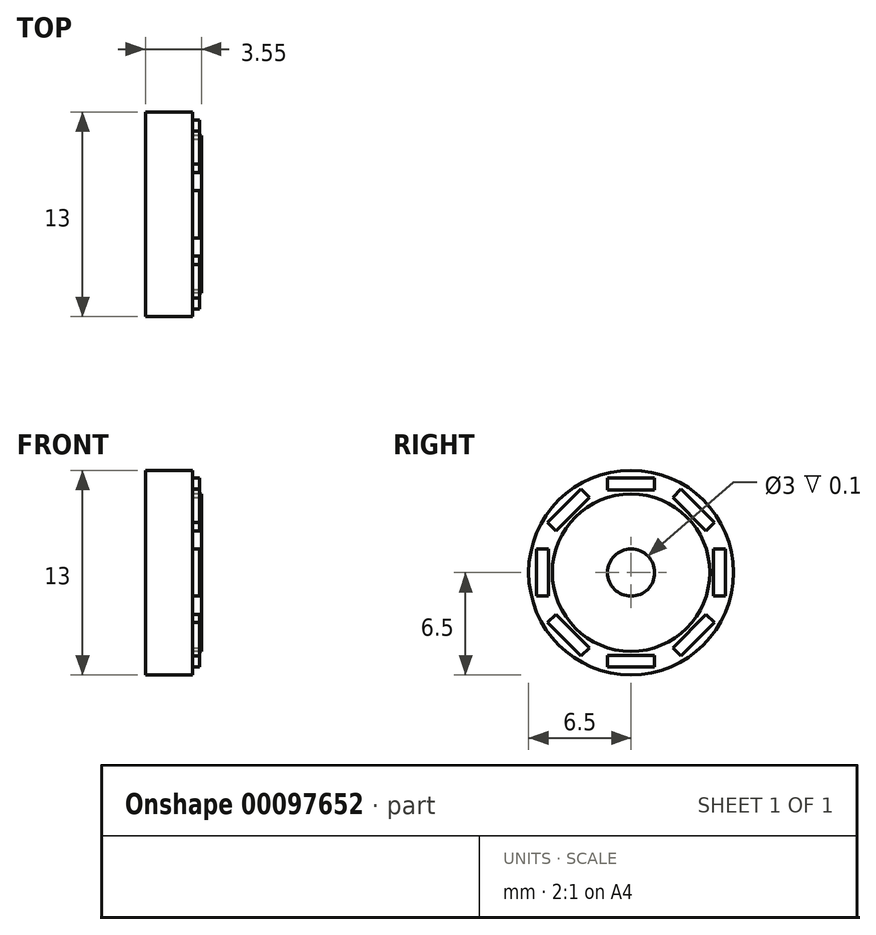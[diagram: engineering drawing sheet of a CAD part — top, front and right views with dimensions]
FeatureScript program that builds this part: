
annotation { "Feature Type Name" : "Feature", "Feature Type Description" : "" }
export const myFeature = defineFeature(function(context is Context, id is Id, definition is map)
    precondition{}
    {
        {
            var Q0;
            Q0=qCreatedBy(makeId("Right.planeOp"),FACE);
            var sketch = newSketch(context, id + "F0", { "sketchPlane" : qUnion([Q0])});
            skCircle(sketch, "E0", {"center": v(0, 0) * mm, "radius": 6.5 * mm});
            skCircle(sketch, "E1", {"center": v(0, 0) * mm, "radius": 5 * mm});
            skCircle(sketch, "E2", {"center": v(0, 0) * mm, "radius": 1.5 * mm});
            skSolve(sketch);
        }
        {
            var Q0;
            Q0=makeQuery(id+"F0.imprint","IMPRINT",FACE,{"disambiguationData":[TD([[makeQuery(id+"F0.imprint","IMPRINT",EDGE,{"derivedFrom":sQuery(id+"F0.wireOp",EDGE,"E0")}),1.0]])]});
            var Q1;
            Q1=makeQuery(id+"F0.imprint","IMPRINT",FACE,{"disambiguationData":[TD([[makeQuery(id+"F0.imprint","IMPRINT",EDGE,{"derivedFrom":sQuery(id+"F0.wireOp",EDGE,"E1")}),1.0]])]});
            var Q2;
            Q2=makeQuery(id+"F0.imprint","IMPRINT",FACE,{"disambiguationData":[TD([[makeQuery(id+"F0.imprint","IMPRINT",EDGE,{"derivedFrom":sQuery(id+"F0.wireOp",EDGE,"E2")}),1.0]])]});
            extrude(context, id + "F1", {"entities" : qUnion([Q0, Q1, Q2]), "depth" : 3 * mm});
        }
        {
            var Q0;
            Q0=makeQuery(id+"F0.imprint","IMPRINT",FACE,{"disambiguationData":[TD([[makeQuery(id+"F0.imprint","IMPRINT",EDGE,{"derivedFrom":sQuery(id+"F0.wireOp",EDGE,"E1")}),1.0]])]});
            extrude(context, id + "F2", {"entities" : qUnion([Q0]), "operationType" : NewBodyOperationType.ADD, "depth" : 3.55 * mm});
        }
        {
            var Q0;
            Q0=makeQuery(id+"F0.imprint","IMPRINT",FACE,{"disambiguationData":[TD([[makeQuery(id+"F0.imprint","IMPRINT",EDGE,{"derivedFrom":sQuery(id+"F0.wireOp",EDGE,"E2")}),1.0]])]});
            extrude(context, id + "F3", {"entities" : qUnion([Q0]), "operationType" : NewBodyOperationType.ADD, "depth" : 3.45 * mm});
        }
        {
            var Q0;
            Q0=makeQuery(id+"F3.opExtrude","CAP_FACE",FACE,{"disambiguationData":[OSD([sQuery(id+"F0.wireOp",EDGE,"E2")])],"isStart":false});
            var sketch = newSketch(context, id + "F4", { "sketchPlane" : qUnion([Q0])});
            skLineSegment(sketch, "E3.bottom", {"start": v(-1.5, 6) * mm, "end": v(1.5, 6) * mm});
            skLineSegment(sketch, "E3.top", {"start": v(-1.5, 5.25) * mm, "end": v(1.5, 5.25) * mm});
            skLineSegment(sketch, "E3.left", {"start": v(-1.5, 6) * mm, "end": v(-1.5, 5.25) * mm});
            skLineSegment(sketch, "E3.right", {"start": v(1.5, 6) * mm, "end": v(1.5, 5.25) * mm});
            skLineSegment(sketch, "E4.1.0", {"start": v(3.18, 5.3) * mm, "end": v(5.3, 3.18) * mm});
            skLineSegment(sketch, "E4.1.1", {"start": v(3.18, 5.3) * mm, "end": v(2.65, 4.77) * mm});
            skLineSegment(sketch, "E4.1.2", {"start": v(5.3, 3.18) * mm, "end": v(4.77, 2.65) * mm});
            skLineSegment(sketch, "E4.1.3", {"start": v(2.65, 4.77) * mm, "end": v(4.77, 2.65) * mm});
            skLineSegment(sketch, "E4.2.0", {"start": v(6, 1.5) * mm, "end": v(6, -1.5) * mm});
            skLineSegment(sketch, "E4.2.1", {"start": v(6, 1.5) * mm, "end": v(5.25, 1.5) * mm});
            skLineSegment(sketch, "E4.2.2", {"start": v(6, -1.5) * mm, "end": v(5.25, -1.5) * mm});
            skLineSegment(sketch, "E4.2.3", {"start": v(5.25, 1.5) * mm, "end": v(5.25, -1.5) * mm});
            skLineSegment(sketch, "E4.3.0", {"start": v(5.3, -3.18) * mm, "end": v(3.18, -5.3) * mm});
            skLineSegment(sketch, "E4.3.1", {"start": v(5.3, -3.18) * mm, "end": v(4.77, -2.65) * mm});
            skLineSegment(sketch, "E4.3.2", {"start": v(3.18, -5.3) * mm, "end": v(2.65, -4.77) * mm});
            skLineSegment(sketch, "E4.3.3", {"start": v(4.77, -2.65) * mm, "end": v(2.65, -4.77) * mm});
            skLineSegment(sketch, "E4.4.0", {"start": v(1.5, -6) * mm, "end": v(-1.5, -6) * mm});
            skLineSegment(sketch, "E4.4.1", {"start": v(1.5, -6) * mm, "end": v(1.5, -5.25) * mm});
            skLineSegment(sketch, "E4.4.2", {"start": v(-1.5, -6) * mm, "end": v(-1.5, -5.25) * mm});
            skLineSegment(sketch, "E4.4.3", {"start": v(1.5, -5.25) * mm, "end": v(-1.5, -5.25) * mm});
            skLineSegment(sketch, "E4.5.0", {"start": v(-3.18, -5.3) * mm, "end": v(-5.3, -3.18) * mm});
            skLineSegment(sketch, "E4.5.1", {"start": v(-3.18, -5.3) * mm, "end": v(-2.65, -4.77) * mm});
            skLineSegment(sketch, "E4.5.2", {"start": v(-5.3, -3.18) * mm, "end": v(-4.77, -2.65) * mm});
            skLineSegment(sketch, "E4.5.3", {"start": v(-2.65, -4.77) * mm, "end": v(-4.77, -2.65) * mm});
            skLineSegment(sketch, "E4.6.0", {"start": v(-6, -1.5) * mm, "end": v(-6, 1.5) * mm});
            skLineSegment(sketch, "E4.6.1", {"start": v(-6, -1.5) * mm, "end": v(-5.25, -1.5) * mm});
            skLineSegment(sketch, "E4.6.2", {"start": v(-6, 1.5) * mm, "end": v(-5.25, 1.5) * mm});
            skLineSegment(sketch, "E4.6.3", {"start": v(-5.25, -1.5) * mm, "end": v(-5.25, 1.5) * mm});
            skLineSegment(sketch, "E4.7.0", {"start": v(-5.3, 3.18) * mm, "end": v(-3.18, 5.3) * mm});
            skLineSegment(sketch, "E4.7.1", {"start": v(-5.3, 3.18) * mm, "end": v(-4.77, 2.65) * mm});
            skLineSegment(sketch, "E4.7.2", {"start": v(-3.18, 5.3) * mm, "end": v(-2.65, 4.77) * mm});
            skLineSegment(sketch, "E4.7.3", {"start": v(-4.77, 2.65) * mm, "end": v(-2.65, 4.77) * mm});
            skPoint(sketch, "E4.center", {"position": v(0, 0) * mm});
            skSolve(sketch);
        }
        {
            var Q0;
            Q0=makeQuery(id+"F4.imprint","IMPRINT",FACE,{"disambiguationData":[TD([[makeQuery(id+"F4.imprint","IMPRINT",EDGE,{"derivedFrom":sQuery(id+"F4.wireOp",EDGE,"E3.bottom")}),-1.0]])]});
            var Q1;
            Q1=makeQuery(id+"F4.imprint","IMPRINT",FACE,{"disambiguationData":[TD([[makeQuery(id+"F4.imprint","IMPRINT",EDGE,{"derivedFrom":sQuery(id+"F4.wireOp",EDGE,"E4.1.0")}),-1.0]])]});
            var Q2;
            Q2=makeQuery(id+"F4.imprint","IMPRINT",FACE,{"disambiguationData":[TD([[makeQuery(id+"F4.imprint","IMPRINT",EDGE,{"derivedFrom":sQuery(id+"F4.wireOp",EDGE,"E4.2.0")}),-1.0]])]});
            var Q3;
            Q3=makeQuery(id+"F4.imprint","IMPRINT",FACE,{"disambiguationData":[TD([[makeQuery(id+"F4.imprint","IMPRINT",EDGE,{"derivedFrom":sQuery(id+"F4.wireOp",EDGE,"E4.3.0")}),-1.0]])]});
            var Q4;
            Q4=makeQuery(id+"F4.imprint","IMPRINT",FACE,{"disambiguationData":[TD([[makeQuery(id+"F4.imprint","IMPRINT",EDGE,{"derivedFrom":sQuery(id+"F4.wireOp",EDGE,"E4.4.0")}),-1.0]])]});
            var Q5;
            Q5=makeQuery(id+"F4.imprint","IMPRINT",FACE,{"disambiguationData":[TD([[makeQuery(id+"F4.imprint","IMPRINT",EDGE,{"derivedFrom":sQuery(id+"F4.wireOp",EDGE,"E4.5.0")}),-1.0]])]});
            var Q6;
            Q6=makeQuery(id+"F4.imprint","IMPRINT",FACE,{"disambiguationData":[TD([[makeQuery(id+"F4.imprint","IMPRINT",EDGE,{"derivedFrom":sQuery(id+"F4.wireOp",EDGE,"E4.6.0")}),-1.0]])]});
            var Q7;
            Q7=makeQuery(id+"F4.imprint","IMPRINT",FACE,{"disambiguationData":[TD([[makeQuery(id+"F4.imprint","IMPRINT",EDGE,{"derivedFrom":sQuery(id+"F4.wireOp",EDGE,"E4.7.0")}),-1.0]])]});
            var Q8;
            {var subQ0=sQuery(id+"F0.wireOp",EDGE,"E0");Q8=makeQuery(id+"F2.boolean.opBoolean","SPLIT",FACE,{"disambiguationData":[TD([makeQuery(id+"F1.opExtrude","SWEPT_FACE",FACE,{"disambiguationData":[OSD([subQ0])]})])],"derivedFrom":makeQuery(id+"F1.opExtrude","CAP_FACE",FACE,{"disambiguationData":[OSD([subQ0])],"isStart":false})});}
            extrude(context, id + "F5", {"entities" : qUnion([Q0, Q1, Q2, Q3, Q4, Q5, Q6, Q7]), "operationType" : NewBodyOperationType.ADD, "endBound" : BoundingType.UP_TO_SURFACE, "oppositeDirection" : true, "endBoundEntityFace" : qUnion([Q8]), "depth" : 3.5 * mm});
        }
    });
